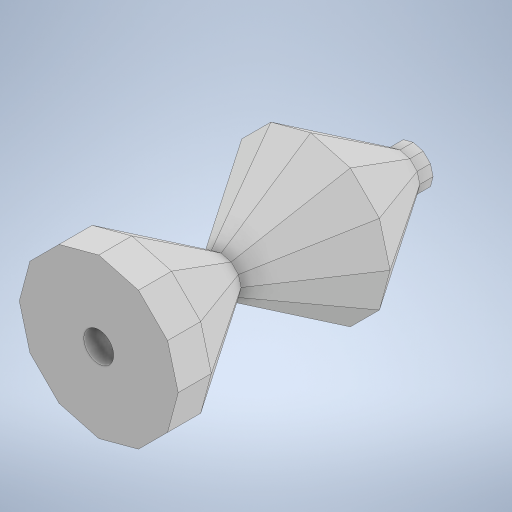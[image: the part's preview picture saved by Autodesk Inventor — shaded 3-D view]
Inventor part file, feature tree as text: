
AUTODESK INVENTOR PART (.ipt)
format: ipt  version: 2023 (Build 270158000, 158)  size: 355,840 bytes
history: native  units: in
note: dims shown in document units (in); Inventor stores cm internally (conversion verified against a paired STEP export)
features: sketch x6, extrude x4, projected_geometry x3, other x2, mirror x2, loft x1, shell x1
ambient origin geometry x8: Origin, YZ Plane, XZ Plane, XY Plane, X Axis, Y Axis, Z Axis, Center Point
bodies: Body1 (feature_tree)
feature tree (19):
  other  "솔리드1"
  sketch  "스케치1"
  other  "작업 평면1"
  loft  "로프트1"
  mirror  "미러1"
  mirror  "미러2"
  extrude  "돌출1"  Depth=0.5315in
  shell  "쉘1"  Thickness=0.2362in
  extrude  "돌출2"  TaperAngle=0.0deg  [1 undecoded]
  extrude  "돌출3"  TaperAngle=0.0deg  [1 undecoded]
  extrude  "돌출4"  Depth=0.0787in TaperAngle=0.0deg
  sketch  "스케치2"
  sketch  "스케치3"
  projected_geometry  "투영된 루프1"
  sketch  "스케치4"
  projected_geometry  "투영된 루프2"
  sketch  "스케치5"
  sketch  "스케치6"
  projected_geometry  "투영된 루프3"
note: 2 required parameter values undecoded (feature->parameter linkage not recoverable at this tier; creation-order binding heuristic only, values carry confidence <= 0.55)
